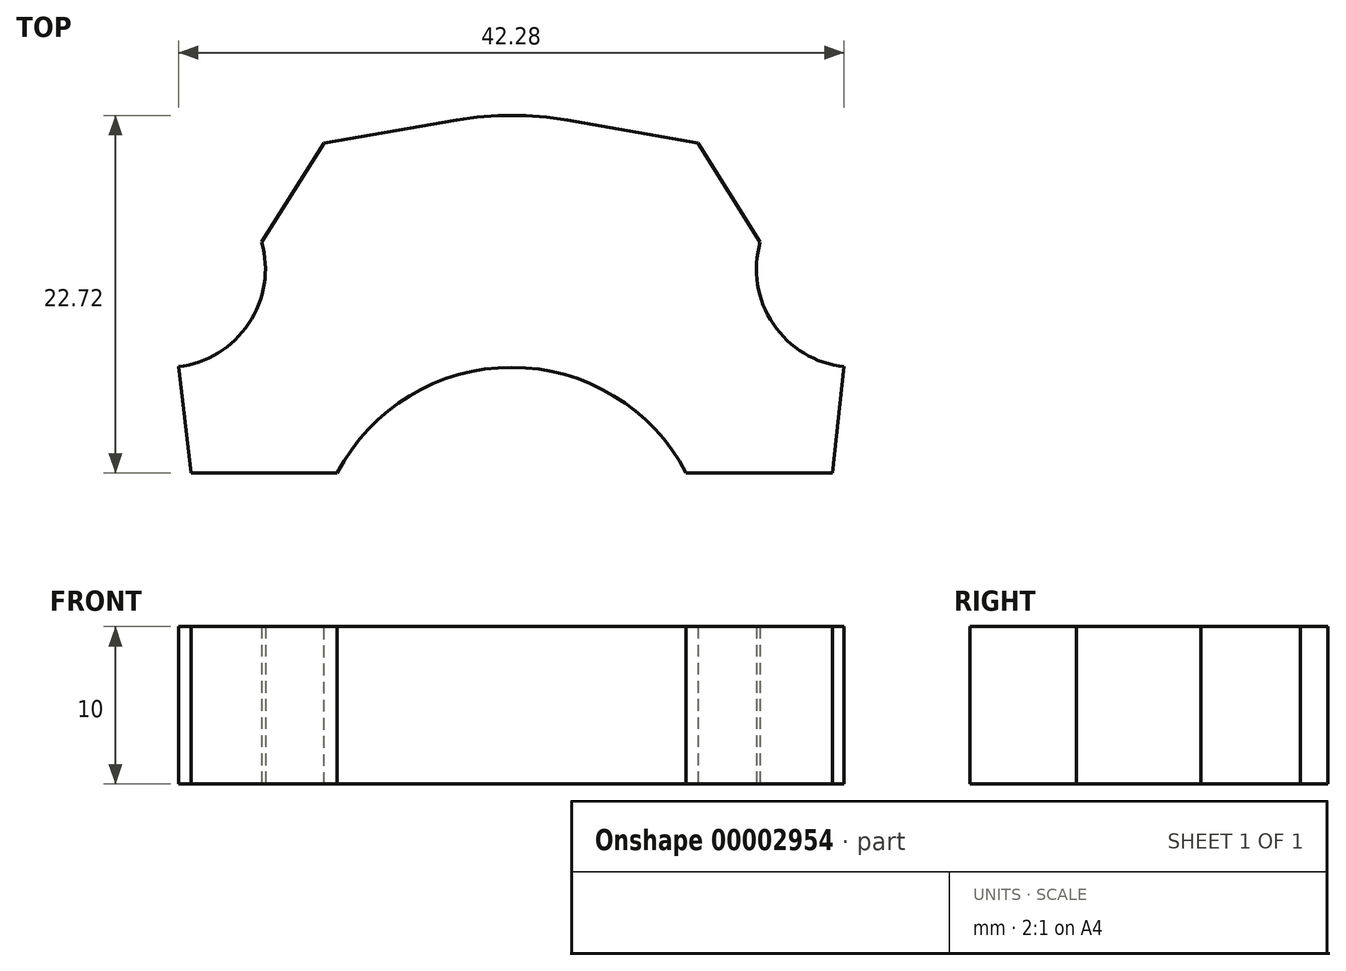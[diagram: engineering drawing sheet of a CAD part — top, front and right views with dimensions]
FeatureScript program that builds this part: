
annotation { "Feature Type Name" : "Feature", "Feature Type Description" : "" }
export const myFeature = defineFeature(function(context is Context, id is Id, definition is map)
    precondition{}
    {
        {
            var Q0;
            Q0=qCreatedBy(makeId("Top.planeOp"),FACE);
            var sketch = newSketch(context, id + "F0", { "sketchPlane" : qUnion([Q0])});
            skLineSegment(sketch, "E0.bottom", {"start": v(0, 0) * mm, "end": v(-20, 0) * mm, "construction": true});
            skLineSegment(sketch, "E0.top", {"start": v(0, 50) * mm, "end": v(-20, 50) * mm, "construction": true});
            skLineSegment(sketch, "E0.left", {"start": v(0, 0) * mm, "end": v(0, 50) * mm, "construction": true});
            skLineSegment(sketch, "E0.right", {"start": v(-20, 0) * mm, "end": v(-20, 12.5) * mm, "construction": true});
            skLineSegment(sketch, "E1.bottom", {"start": v(0, 0) * mm, "end": v(20, 0) * mm, "construction": true});
            skLineSegment(sketch, "E1.top", {"start": v(0, 50) * mm, "end": v(20, 50) * mm, "construction": true});
            skLineSegment(sketch, "E1.left", {"start": v(0, 0) * mm, "end": v(0, 12.5) * mm, "construction": true});
            skLineSegment(sketch, "E1.right", {"start": v(20, 0) * mm, "end": v(20, 12.5) * mm, "construction": true});
            skLineSegment(sketch, "E2.top", {"start": v(0, -54.73) * mm, "end": v(-20, -54.73) * mm, "construction": true});
            skLineSegment(sketch, "E2.left", {"start": v(0, 0) * mm, "end": v(0, -54.73) * mm, "construction": true});
            skLineSegment(sketch, "E2.right", {"start": v(-20, 0) * mm, "end": v(-20, -27.37) * mm, "construction": true});
            skLineSegment(sketch, "E3.top", {"start": v(0, -54.73) * mm, "end": v(20, -54.73) * mm, "construction": true});
            skLineSegment(sketch, "E3.left", {"start": v(0, 0) * mm, "end": v(0, -27.37) * mm, "construction": true});
            skLineSegment(sketch, "E3.right", {"start": v(20, 0) * mm, "end": v(20, -27.37) * mm, "construction": true});
            skLineSegment(sketch, "E4", {"start": v(0, 25) * mm, "end": v(0, 37.5) * mm, "construction": true});
            skLineSegment(sketch, "E5", {"start": v(20, 25) * mm, "end": v(20, 37.5) * mm, "construction": true});
            skLineSegment(sketch, "E6", {"start": v(-20, 25) * mm, "end": v(-20, 37.5) * mm, "construction": true});
            skLineSegment(sketch, "E7", {"start": v(0, 12.5) * mm, "end": v(0, 25) * mm, "construction": true});
            skLineSegment(sketch, "E8", {"start": v(20, 12.5) * mm, "end": v(20, 25) * mm, "construction": true});
            skLineSegment(sketch, "E9", {"start": v(-20, 12.5) * mm, "end": v(-20, 25) * mm, "construction": true});
            skLineSegment(sketch, "E10", {"start": v(0, -27.37) * mm, "end": v(0, -54.73) * mm, "construction": true});
            skLineSegment(sketch, "E11", {"start": v(20, -27.37) * mm, "end": v(20, -54.73) * mm, "construction": true});
            skLineSegment(sketch, "E12", {"start": v(-20, -27.37) * mm, "end": v(-20, -54.73) * mm, "construction": true});
            skLineSegment(sketch, "E13", {"start": v(0, 37.5) * mm, "end": v(0, 50) * mm, "construction": true});
            skLineSegment(sketch, "E14", {"start": v(20, 37.5) * mm, "end": v(20, 50) * mm, "construction": true});
            skLineSegment(sketch, "E15", {"start": v(-20, 37.5) * mm, "end": v(-20, 50) * mm, "construction": true});
            skLineSegment(sketch, "E16.bottom", {"start": v(0, 0) * mm, "end": v(20, 0) * mm});
            skLineSegment(sketch, "E16.top", {"start": v(0, 12.5) * mm, "end": v(20, 12.5) * mm});
            skLineSegment(sketch, "E16.left", {"start": v(0, 0) * mm, "end": v(0, 12.5) * mm});
            skLineSegment(sketch, "E16.right", {"start": v(20, 0) * mm, "end": v(20, 12.5) * mm});
            skLineSegment(sketch, "E17.bottom", {"start": v(0, 0) * mm, "end": v(-20, 0) * mm});
            skLineSegment(sketch, "E17.top", {"start": v(0, 12.5) * mm, "end": v(-20, 12.5) * mm});
            skLineSegment(sketch, "E17.right", {"start": v(-20, 0) * mm, "end": v(-20, 12.5) * mm});
            skCircle(sketch, "E18", {"center": v(-15, 3.13) * mm, "radius": 5.9 * mm});
            skPoint(sketch, "E18.first.point", {"position": v(-10, 0) * mm});
            skPoint(sketch, "E18.third.point", {"position": v(-20, 6.25) * mm});
            skCircle(sketch, "E19", {"center": v(15, 3.12) * mm, "radius": 5.9 * mm});
            skPoint(sketch, "E19.first.point", {"position": v(10, 0) * mm});
            skPoint(sketch, "E19.third.point", {"position": v(20, 6.25) * mm});
            skCircle(sketch, "E20", {"center": v(0, 20.5) * mm, "radius": 20.5 * mm});
            skLineSegment(sketch, "E21.bottom", {"start": v(0, 31.25) * mm, "end": v(21.8, 31.25) * mm});
            skLineSegment(sketch, "E21.top", {"start": v(0, 37.5) * mm, "end": v(21.8, 37.5) * mm});
            skLineSegment(sketch, "E21.left", {"start": v(0, 31.25) * mm, "end": v(0, 37.5) * mm});
            skLineSegment(sketch, "E21.right", {"start": v(21.8, 31.25) * mm, "end": v(21.8, 37.5) * mm});
            skLineSegment(sketch, "E22.bottom", {"start": v(0, 31.25) * mm, "end": v(-18.15, 31.25) * mm});
            skLineSegment(sketch, "E22.top", {"start": v(0, 37.5) * mm, "end": v(-21.9, 37.5) * mm});
            skLineSegment(sketch, "E22.right", {"start": v(-21.9, 31.25) * mm, "end": v(-21.9, 35) * mm});
            skLineSegment(sketch, "E23", {"start": v(21.8, 31.25) * mm, "end": v(20.38, 18.28) * mm});
            skLineSegment(sketch, "E24", {"start": v(20.38, 18.28) * mm, "end": v(-20.38, 18.28) * mm});
            skLineSegment(sketch, "E25", {"start": v(-20.38, 18.28) * mm, "end": v(-21.9, 31.25) * mm});
            skLineSegment(sketch, "E26", {"start": v(-21.9, 37.5) * mm, "end": v(-3.51, 40.7) * mm});
            skLineSegment(sketch, "E27", {"start": v(21.8, 37.5) * mm, "end": v(3.53, 40.7) * mm});
            skCircle(sketch, "E28", {"center": v(21.8, 31.25) * mm, "radius": 6.25 * mm});
            skCircle(sketch, "E29", {"center": v(-21.9, 31.25) * mm, "radius": 6.25 * mm});
            skLineSegment(sketch, "E30.bottom", {"start": v(-15, 3.13) * mm, "end": v(-10, 3.13) * mm});
            skLineSegment(sketch, "E30.top", {"start": v(-15, -27.37) * mm, "end": v(-10, -27.37) * mm});
            skLineSegment(sketch, "E30.left", {"start": v(-15, 3.13) * mm, "end": v(-15, -27.37) * mm});
            skLineSegment(sketch, "E30.right", {"start": v(-10, 3.13) * mm, "end": v(-10, -27.37) * mm});
            skLineSegment(sketch, "E31.bottom", {"start": v(15, 3.12) * mm, "end": v(10, 3.12) * mm});
            skLineSegment(sketch, "E31.top", {"start": v(15, -27.37) * mm, "end": v(10, -27.37) * mm});
            skLineSegment(sketch, "E31.left", {"start": v(15, 3.12) * mm, "end": v(15, -27.37) * mm});
            skLineSegment(sketch, "E31.right", {"start": v(10, 3.12) * mm, "end": v(10, -27.37) * mm});
            skLineSegment(sketch, "E32", {"start": v(-20, 0) * mm, "end": v(-15, -27.37) * mm});
            skLineSegment(sketch, "E33", {"start": v(20, 0) * mm, "end": v(15, -27.37) * mm});
            skLineSegment(sketch, "E34", {"start": v(10, -54.73) * mm, "end": v(10, -27.37) * mm});
            skLineSegment(sketch, "E35", {"start": v(15, -27.37) * mm, "end": v(15, -54.73) * mm});
            skLineSegment(sketch, "E36", {"start": v(15, -54.73) * mm, "end": v(10, -54.73) * mm});
            skLineSegment(sketch, "E37", {"start": v(-15, -27.37) * mm, "end": v(-15, -54.73) * mm});
            skLineSegment(sketch, "E38", {"start": v(-15, -54.73) * mm, "end": v(-10, -54.73) * mm});
            skLineSegment(sketch, "E39", {"start": v(-10, -54.73) * mm, "end": v(-10, -27.37) * mm});
            skCircle(sketch, "E40", {"center": v(-12.5, -27.37) * mm, "radius": 2.5 * mm});
            skCircle(sketch, "E41", {"center": v(12.5, -27.37) * mm, "radius": 2.46 * mm});
            skLineSegment(sketch, "E42", {"start": v(12.5, -27.37) * mm, "end": v(12.5, -24.9) * mm});
            skCircle(sketch, "E43", {"center": v(12.5, -24.9) * mm, "radius": 2.46 * mm});
            skCircle(sketch, "E44", {"center": v(12.5, -29.83) * mm, "radius": 2.46 * mm});
            skLineSegment(sketch, "E45", {"start": v(12.5, -29.83) * mm, "end": v(12.5, -27.37) * mm});
            skCircle(sketch, "E46", {"center": v(0, 12.5) * mm, "radius": 12.5 * mm});
            skLineSegment(sketch, "E47", {"start": v(-21.9, 31.25) * mm, "end": v(-21.9, 27.5) * mm});
            skLineSegment(sketch, "E48", {"start": v(-21.9, 35) * mm, "end": v(-21.9, 36.25) * mm});
            skLineSegment(sketch, "E49", {"start": v(-21.9, 36.25) * mm, "end": v(-21.9, 37.5) * mm});
            skLineSegment(sketch, "E50", {"start": v(-21.9, 27.5) * mm, "end": v(-21.9, 25) * mm});
            skLineSegment(sketch, "E51", {"start": v(-21.9, 31.25) * mm, "end": v(-26.9, 31.25) * mm});
            skLineSegment(sketch, "E52", {"start": v(-26.9, 31.25) * mm, "end": v(-26.9, 36.25) * mm});
            skLineSegment(sketch, "E53", {"start": v(-26.9, 36.25) * mm, "end": v(-21.9, 36.25) * mm});
            skLineSegment(sketch, "E54", {"start": v(-21.9, 26.25) * mm, "end": v(-26.9, 26.25) * mm});
            skLineSegment(sketch, "E55", {"start": v(-26.9, 26.25) * mm, "end": v(-26.9, 31.25) * mm});
            skLineSegment(sketch, "E56", {"start": v(-18.15, 31.25) * mm, "end": v(-20.02, 31.25) * mm});
            skLineSegment(sketch, "E57", {"start": v(-20.02, 31.25) * mm, "end": v(-21.9, 31.25) * mm});
            skArc(sketch, "E58", {"start": v(-20, 34.48) * mm, "mid": v(-25.65, 31.25) * mm, "end": v(-20, 28.02) * mm});
            skArc(sketch, "E59", {"start": v(-20, 28.02) * mm, "mid": v(-18.15, 31.25) * mm, "end": v(-20, 34.48) * mm});
            skArc(sketch, "E60", {"start": v(-20, 35.88) * mm, "mid": v(-26.9, 31.25) * mm, "end": v(-20, 26.62) * mm});
            skArc(sketch, "E61", {"start": v(-20, 26.62) * mm, "mid": v(-16.9, 31.25) * mm, "end": v(-20, 35.88) * mm});
            skLineSegment(sketch, "E62", {"start": v(-20, 35.88) * mm, "end": v(-20, 34.48) * mm});
            skLineSegment(sketch, "E63", {"start": v(-20, 28.02) * mm, "end": v(-20, 26.62) * mm});
            skLineSegment(sketch, "E64", {"start": v(-20, 34.48) * mm, "end": v(-20.02, 31.25) * mm});
            skLineSegment(sketch, "E65", {"start": v(-20, 28.02) * mm, "end": v(-20.02, 31.25) * mm});
            skSolve(sketch);
        }
        {
            var Q0;
            {var subQ5=sQuery(id+"F0.wireOp",EDGE,"E21.left");Q0=makeQuery(id+"F0.imprint","IMPRINT",FACE,{"disambiguationData":[TD([[makeQuery(id+"F0.imprint","IMPRINT",EDGE,{"derivedFrom":subQ5}),1.0]])]});}
            var Q1;
            {var subQ1=sQuery(id+"F0.wireOp",EDGE,"E20");var subQ3=sQuery(id+"F0.wireOp",EDGE,"E22.top");var subQ5=makeQuery(id+"F0.imprint","INTERSECT",VERTEX,{"derivedFrom":[subQ1,subQ3]});Q1=makeQuery(id+"F0.imprint","IMPRINT",FACE,{"disambiguationData":[TD([[makeQuery(id+"F0.imprint","IMPRINT",EDGE,{"disambiguationData":[TD([[subQ5,-1.0]])],"derivedFrom":subQ1}),-1.0]])]});}
            var Q2;
            {var subQ0=sQuery(id+"F0.wireOp",EDGE,"E26");Q2=makeQuery(id+"F0.imprint","IMPRINT",FACE,{"disambiguationData":[TD([[makeQuery(id+"F0.imprint","IMPRINT",EDGE,{"derivedFrom":subQ0}),-1.0]])]});}
            var Q3;
            {var subQ1=sQuery(id+"F0.wireOp",EDGE,"E20");var subQ7=makeQuery(id+"F0.imprint","INTERSECT",VERTEX,{"derivedFrom":[subQ1,sQuery(id+"F0.wireOp",EDGE,"E27")]});Q3=makeQuery(id+"F0.imprint","IMPRINT",FACE,{"disambiguationData":[TD([[makeQuery(id+"F0.imprint","IMPRINT",EDGE,{"disambiguationData":[TD([[subQ7,1.0]])],"derivedFrom":subQ1}),1.0]])]});}
            var Q4;
            {var subQ7=sQuery(id+"F0.wireOp",EDGE,"E20");var subQ11=sQuery(id+"F0.wireOp",EDGE,"E28");var subQ15=makeQuery(id+"F0.imprint","INTERSECT",VERTEX,{"disambiguationData":[OD(0.0)],"derivedFrom":[subQ7,subQ11]});Q4=makeQuery(id+"F0.imprint","IMPRINT",FACE,{"disambiguationData":[TD([[makeQuery(id+"F0.imprint","IMPRINT",EDGE,{"disambiguationData":[TD([[subQ15,1.0]])],"derivedFrom":subQ11}),-1.0]])]});}
            var Q5;
            {var subQ0=sQuery(id+"F0.wireOp",EDGE,"E29");var subQ3=sQuery(id+"F0.wireOp",EDGE,"E25");var subQ4=makeQuery(id+"F0.imprint","INTERSECT",VERTEX,{"derivedFrom":[subQ3,subQ0]});Q5=makeQuery(id+"F0.imprint","IMPRINT",FACE,{"disambiguationData":[TD([[makeQuery(id+"F0.imprint","IMPRINT",EDGE,{"disambiguationData":[TD([[subQ4,-1.0]])],"derivedFrom":subQ0}),-1.0]])]});}
            var Q6;
            {var subQ5=sQuery(id+"F0.wireOp",EDGE,"E21.left");Q6=makeQuery(id+"F0.imprint","IMPRINT",FACE,{"disambiguationData":[TD([[makeQuery(id+"F0.imprint","IMPRINT",EDGE,{"derivedFrom":subQ5}),-1.0]])]});}
            var Q7;
            {var subQ0=sQuery(id+"F0.wireOp",EDGE,"E27");Q7=makeQuery(id+"F0.imprint","IMPRINT",FACE,{"disambiguationData":[TD([[makeQuery(id+"F0.imprint","IMPRINT",EDGE,{"derivedFrom":subQ0}),1.0]])]});}
            var Q8;
            {var subQ0=sQuery(id+"F0.wireOp",EDGE,"E28");var subQ1=sQuery(id+"F0.wireOp",EDGE,"E20");var subQ2=makeQuery(id+"F0.imprint","INTERSECT",VERTEX,{"disambiguationData":[OD(1.0)],"derivedFrom":[subQ1,subQ0]});Q8=makeQuery(id+"F0.imprint","IMPRINT",FACE,{"disambiguationData":[TD([[makeQuery(id+"F0.imprint","IMPRINT",EDGE,{"disambiguationData":[TD([[subQ2,-1.0]])],"derivedFrom":subQ1}),-1.0]])]});}
            var Q9;
            {var subQ0=sQuery(id+"F0.wireOp",EDGE,"E28");var subQ3=sQuery(id+"F0.wireOp",EDGE,"E23");var subQ4=makeQuery(id+"F0.imprint","INTERSECT",VERTEX,{"derivedFrom":[subQ3,subQ0]});Q9=makeQuery(id+"F0.imprint","IMPRINT",FACE,{"disambiguationData":[TD([[makeQuery(id+"F0.imprint","IMPRINT",EDGE,{"disambiguationData":[TD([[subQ4,1.0]])],"derivedFrom":subQ0}),-1.0]])]});}
            extrude(context, id + "F1", {"entities" : qUnion([Q0, Q1, Q2, Q3, Q4, Q5, Q6, Q7, Q8, Q9]), "endBound" : BoundingType.SYMMETRIC, "depth" : 10 * mm});
        }
        {
            var Q0;
            Q0=makeQuery(id+"F1.opExtrude","SWEPT_EDGE",EDGE,{"disambiguationData":[OSD([sQuery(id+"F0.wireOp",EDGE,"E21.top"),sQuery(id+"F0.wireOp",EDGE,"E21.right"),sQuery(id+"F0.wireOp",EDGE,"E27"),sQuery(id+"F0.wireOp",EDGE,"E28")])]});
            var Q1;
            Q1=makeQuery(id+"F1.opExtrude","SWEPT_EDGE",EDGE,{"disambiguationData":[OSD([sQuery(id+"F0.wireOp",EDGE,"E22.top"),sQuery(id+"F0.wireOp",EDGE,"E22.right"),sQuery(id+"F0.wireOp",EDGE,"E26"),sQuery(id+"F0.wireOp",EDGE,"E29")])]});
            chamfer(context, id + "F2", {"entities" : qUnion([Q0, Q1]), "width" : 5 * mm, "tangentPropagation" : true});
        }
        {
            var Q0;
            {var subQ0=sQuery(id+"F0.wireOp",EDGE,"E47");Q0=makeQuery(id+"F0.imprint","IMPRINT",FACE,{"disambiguationData":[TD([[makeQuery(id+"F0.imprint","IMPRINT",EDGE,{"derivedFrom":subQ0}),-1.0]])]});}
            var Q1;
            Q1=sQuery(id+"F0.wireOp",EDGE,"E22.right");
            revolve(context, id + "F3", {"entities" : qUnion([Q0]), "axis" : qUnion([Q1]), "revolveType" : RevolveType.FULL});
        }
        {
            var Q0;
            Q0=makeQuery(id+"F3.opRevolve","SWEPT_BODY",BODY,{"disambiguationData":[OSD([sQuery(id+"F0.wireOp",EDGE,"E47"),sQuery(id+"F0.wireOp",EDGE,"E51"),sQuery(id+"F0.wireOp",EDGE,"E58")])]});
            deleteBodies(context, id + "F4", {"entities" : qUnion([Q0])});
        }
    });
